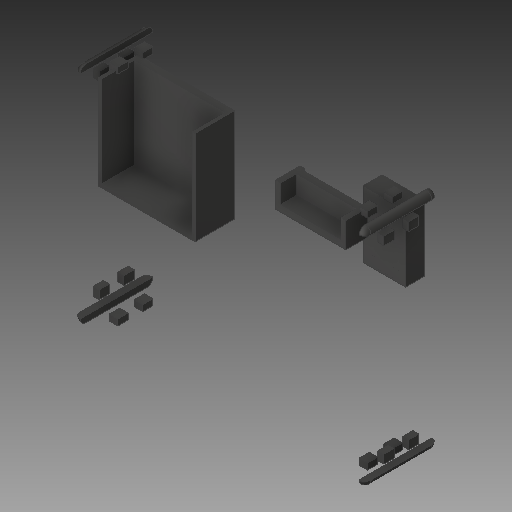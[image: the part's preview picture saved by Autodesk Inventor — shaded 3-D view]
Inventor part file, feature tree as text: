
AUTODESK INVENTOR PART (.ipt)
format: ipt  version: 2018 (Build 220112000, 112)  size: 223,232 bytes
history: native  units: mm
features: other x17, fillet x4
ambient origin geometry x8: Origin, YZ Plane, XZ Plane, XY Plane, X Axis, Y Axis, Z Axis, Center Point
bodies: Solid1 (feature_tree), Solid2 (feature_tree), Solid3 (feature_tree), Solid4 (feature_tree), Solid5 (feature_tree), Solid6 (feature_tree), Solid7 (feature_tree), Solid8 (feature_tree), Solid9 (feature_tree), Solid10 (feature_tree), Solid11 (feature_tree), Solid12 (feature_tree), Solid13 (feature_tree), Solid14 (feature_tree), Solid15 (feature_tree), Solid16 (feature_tree), Solid17 (feature_tree), Solid18 (feature_tree), Solid19 (feature_tree), Solid20 (feature_tree), Solid21 (feature_tree)
feature tree (21):
  fillet  "Fillet1"  [1 undecoded]
  fillet  "Fillet2"  [1 undecoded]
  fillet  "Fillet3"  [1 undecoded]
  fillet  "Fillet4"  [1 undecoded]
  other  "Cut-Extrude3[2]"
  other  "Cut-Extrude3[4]"
  other  "Cut-Extrude3[5]"
  other  "Cut-Extrude3[6]"
  other  "Cut-Extrude3[7]"
  other  "Cut-Extrude3[8]"
  other  "Cut-Extrude3[9]"
  other  "Cut-Extrude3[10]"
  other  "Cut-Extrude3[11]"
  other  "Cut-Extrude3[12]"
  other  "Cut-Extrude3[13]"
  other  "Cut-Extrude3[14]"
  other  "Cut-Extrude3[15]"
  other  "Cut-Extrude3[16]"
  other  "Cut-Extrude3[17]"
  other  "Boss-Extrude10"
  other  "Boss-Extrude11"
note: 4 required parameter values undecoded (feature->parameter linkage not recoverable at this tier; creation-order binding heuristic only, values carry confidence <= 0.55)
